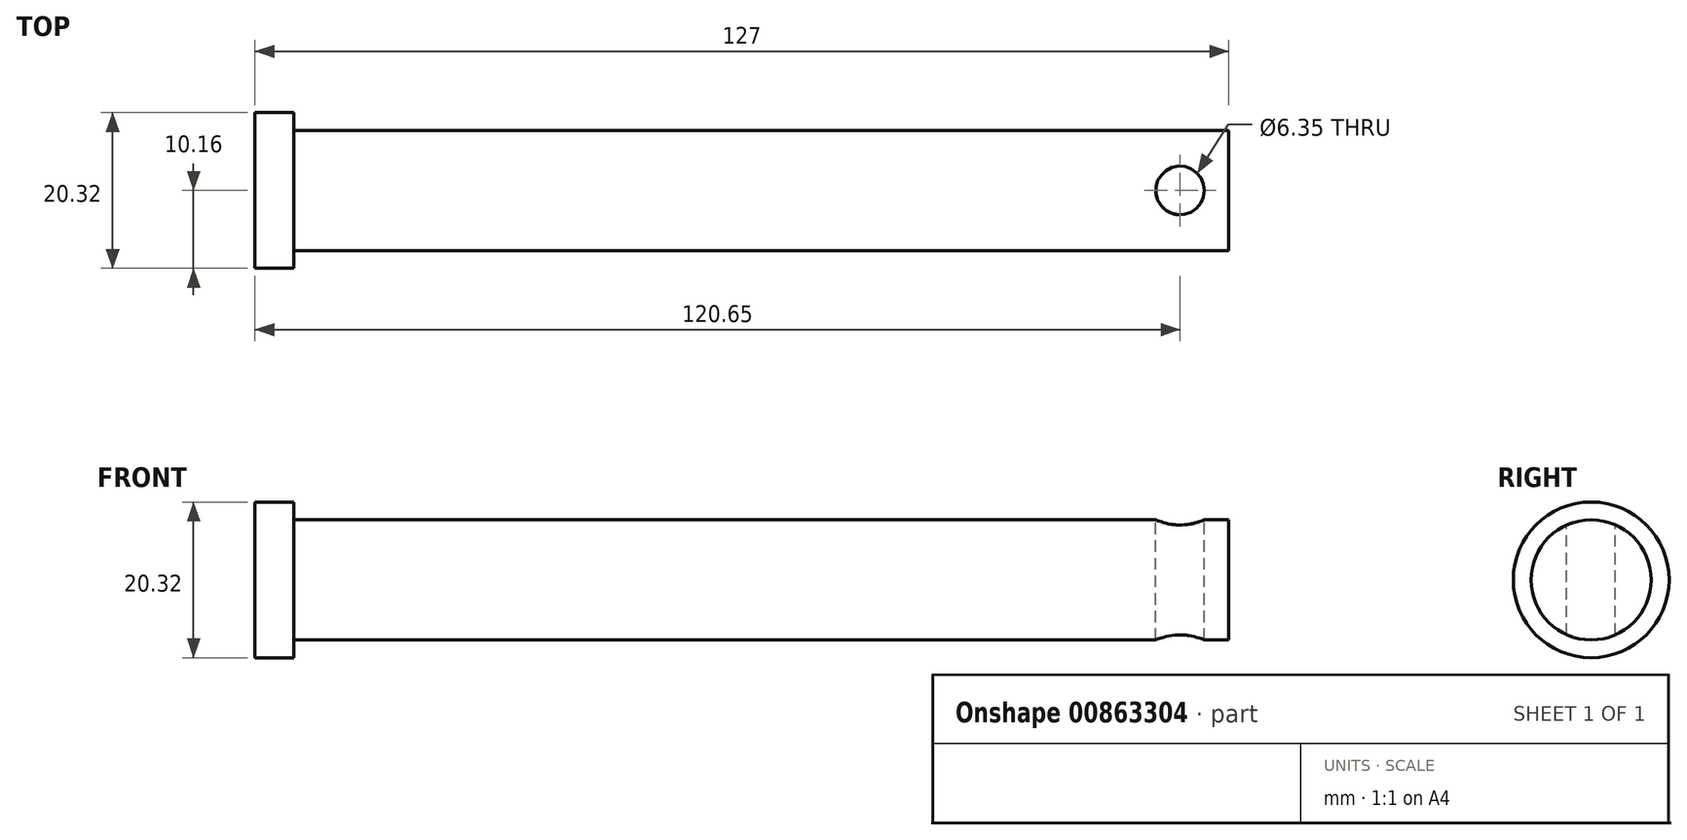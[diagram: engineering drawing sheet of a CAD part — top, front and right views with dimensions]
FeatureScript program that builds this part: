
annotation { "Feature Type Name" : "Feature", "Feature Type Description" : "" }
export const myFeature = defineFeature(function(context is Context, id is Id, definition is map)
    precondition{}
    {
        {
            var Q0;
            Q0=qCreatedBy(makeId("Front.planeOp"),FACE);
            var sketch = newSketch(context, id + "F0", { "sketchPlane" : qUnion([Q0])});
            skLineSegment(sketch, "E0", {"start": v(0, -7.84) * mm, "end": v(-121.92, -7.84) * mm});
            skLineSegment(sketch, "E1", {"start": v(-127, 0) * mm, "end": v(-127, -10.16) * mm});
            skLineSegment(sketch, "E2", {"start": v(-127, -10.16) * mm, "end": v(-121.92, -10.16) * mm});
            skLineSegment(sketch, "E3", {"start": v(-121.92, -10.16) * mm, "end": v(-121.92, -7.84) * mm});
            skLineSegment(sketch, "E4", {"start": v(0, 0) * mm, "end": v(0, -7.84) * mm});
            skLineSegment(sketch, "E5", {"start": v(0, 0) * mm, "end": v(-127, 0) * mm});
            skSolve(sketch);
        }
        {
            var Q0;
            Q0=makeQuery(id+"F0.imprint","IMPRINT",FACE,{"disambiguationData":[TD([[makeQuery(id+"F0.imprint","IMPRINT",EDGE,{"derivedFrom":sQuery(id+"F0.wireOp",EDGE,"E0")}),-1.0]])]});
            var Q1;
            Q1=sQuery(id+"F0.wireOp",EDGE,"E5");
            revolve(context, id + "F1", {"surfaceOperationType" : NewSurfaceOperationType.NEW, "entities" : qUnion([Q0]), "axis" : qUnion([Q1]), "revolveType" : RevolveType.ONE_DIRECTION, "angle" : 0 * degree});
        }
        {
            var Q0;
            Q0=qCreatedBy(makeId("Top.planeOp"),FACE);
            var sketch = newSketch(context, id + "F2", { "sketchPlane" : qUnion([Q0])});
            skCircle(sketch, "E6", {"center": v(-6.35, 0) * mm, "radius": 3.18 * mm});
            skSolve(sketch);
        }
        {
            var Q0;
            Q0 = qSketchRegion(id + "F2", true);
            extrude(context, id + "F3", {"entities" : qUnion([Q0]), "operationType" : NewBodyOperationType.REMOVE, "endBound" : BoundingType.THROUGH_ALL, "oppositeDirection" : true, "depth" : 25.4 * mm, "offsetDistance" : 25.4 * mm, "hasSecondDirection" : true, "secondDirectionBound" : BoundingType.THROUGH_ALL, "secondDirectionOppositeDirection" : false, "secondDirectionDepth" : 25.4 * mm});
        }
    });
